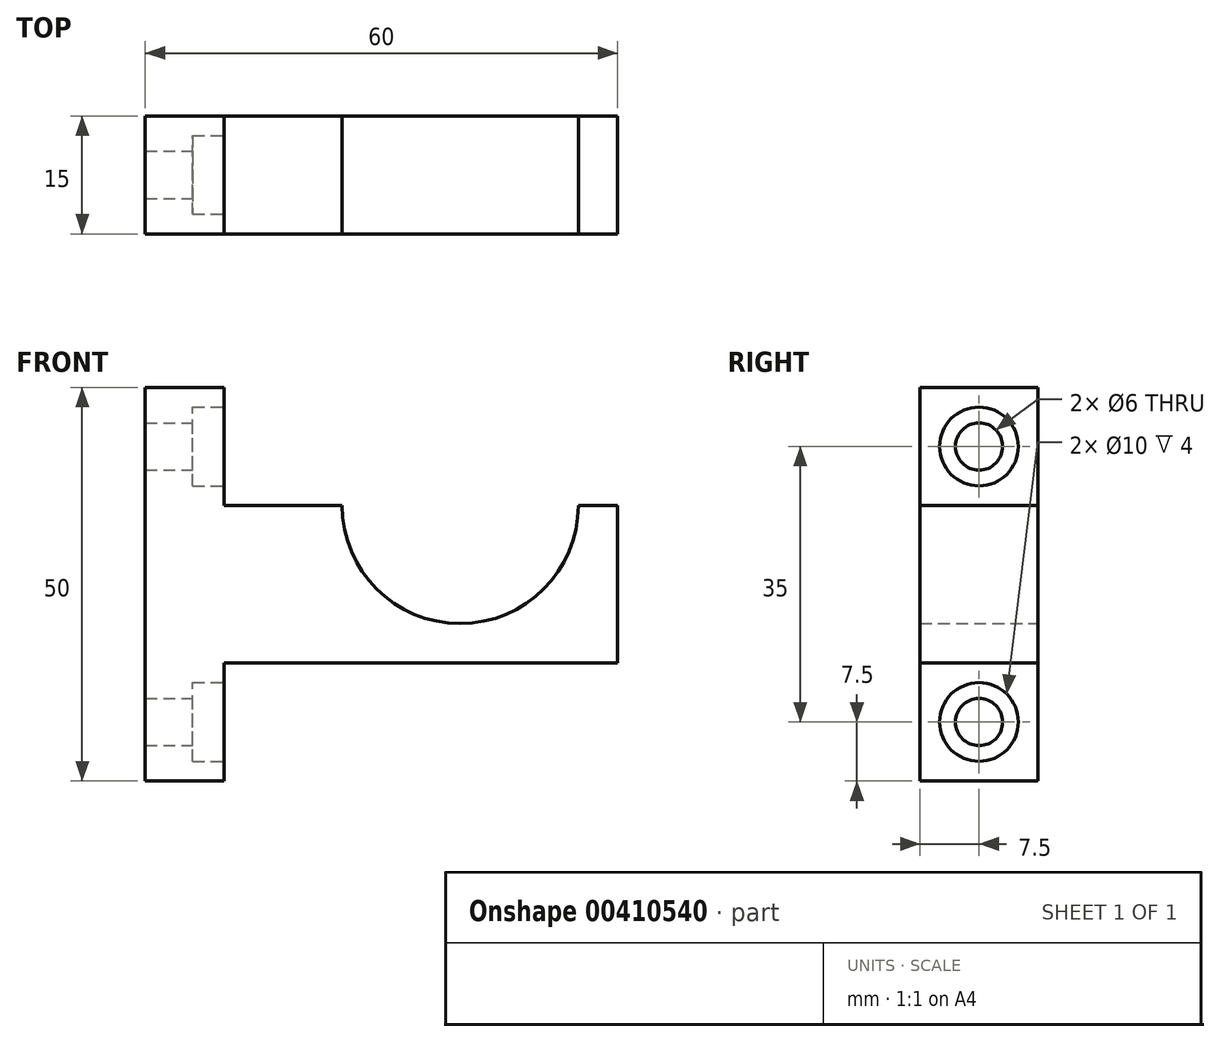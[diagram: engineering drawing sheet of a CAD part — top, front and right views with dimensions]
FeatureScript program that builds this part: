
annotation { "Feature Type Name" : "Feature", "Feature Type Description" : "" }
export const myFeature = defineFeature(function(context is Context, id is Id, definition is map)
    precondition{}
    {
        {
            var Q0;
            Q0=qCreatedBy(makeId("Front.planeOp"),FACE);
            var sketch = newSketch(context, id + "F0", { "sketchPlane" : qUnion([Q0])});
            skLineSegment(sketch, "E0.bottom", {"start": v(30, -25) * mm, "end": v(-30, -25) * mm});
            skLineSegment(sketch, "E0.top", {"start": v(30, 25) * mm, "end": v(-30, 25) * mm});
            skLineSegment(sketch, "E0.left", {"start": v(30, -25) * mm, "end": v(30, 25) * mm});
            skLineSegment(sketch, "E0.right", {"start": v(-30, -25) * mm, "end": v(-30, 25) * mm});
            skPoint(sketch, "E0.middle", {"position": v(0, 0) * mm});
            skPoint(sketch, "E1", {"position": v(10, 10) * mm});
            skCircle(sketch, "E2", {"center": v(10, 10) * mm, "radius": 15 * mm});
            skLineSegment(sketch, "E3", {"start": v(-30, 10) * mm, "end": v(30, 10) * mm});
            skLineSegment(sketch, "E4", {"start": v(-30, -10) * mm, "end": v(30, -10) * mm});
            skLineSegment(sketch, "E5", {"start": v(-20, 25) * mm, "end": v(-20, -25) * mm});
            skSolve(sketch);
        }
        {
            var Q0;
            {var subQ0=sQuery(id+"F0.wireOp",EDGE,"E0.right");var subQ1=sQuery(id+"F0.wireOp",EDGE,"E0.top");var subQ2=makeQuery(id+"F0.imprint","INTERSECT",VERTEX,{"derivedFrom":[subQ1,subQ0]});Q0=makeQuery(id+"F0.imprint","IMPRINT",FACE,{"disambiguationData":[TD([[makeQuery(id+"F0.imprint","IMPRINT",EDGE,{"disambiguationData":[TD([[subQ2,1.0]])],"derivedFrom":subQ1}),1.0]])]});}
            var Q1;
            {var subQ0=sQuery(id+"F0.wireOp",EDGE,"E3");var subQ1=sQuery(id+"F0.wireOp",EDGE,"E0.right");var subQ2=makeQuery(id+"F0.imprint","INTERSECT",VERTEX,{"derivedFrom":[subQ1,subQ0]});Q1=makeQuery(id+"F0.imprint","IMPRINT",FACE,{"disambiguationData":[TD([[makeQuery(id+"F0.imprint","IMPRINT",EDGE,{"disambiguationData":[TD([[subQ2,1.0]])],"derivedFrom":subQ1}),-1.0]])]});}
            var Q2;
            {var subQ0=sQuery(id+"F0.wireOp",EDGE,"E3");var subQ1=sQuery(id+"F0.wireOp",EDGE,"E0.left");var subQ2=makeQuery(id+"F0.imprint","INTERSECT",VERTEX,{"derivedFrom":[subQ1,subQ0]});Q2=makeQuery(id+"F0.imprint","IMPRINT",FACE,{"disambiguationData":[TD([[makeQuery(id+"F0.imprint","IMPRINT",EDGE,{"disambiguationData":[TD([[subQ2,1.0]])],"derivedFrom":subQ1}),1.0]])]});}
            var Q3;
            {var subQ0=sQuery(id+"F0.wireOp",EDGE,"E0.right");var subQ1=sQuery(id+"F0.wireOp",EDGE,"E0.bottom");var subQ2=makeQuery(id+"F0.imprint","INTERSECT",VERTEX,{"derivedFrom":[subQ1,subQ0]});Q3=makeQuery(id+"F0.imprint","IMPRINT",FACE,{"disambiguationData":[TD([[makeQuery(id+"F0.imprint","IMPRINT",EDGE,{"disambiguationData":[TD([[subQ2,1.0]])],"derivedFrom":subQ1}),-1.0]])]});}
            extrude(context, id + "F1", {"entities" : qUnion([Q0, Q1, Q2, Q3]), "depth" : 15 * mm});
        }
        {
            var Q0;
            {var subQ0=sQuery(id+"F0.wireOp",EDGE,"E5");Q0=makeQuery(id+"F1.opExtrude","SWEPT_FACE",FACE,{"disambiguationData":[OSD([subQ0]),TDD([makeQuery(id+"F0.imprint","IMPRINT",EDGE,{"disambiguationData":[TD([[makeQuery(id+"F0.imprint","INTERSECT",VERTEX,{"derivedFrom":[sQuery(id+"F0.wireOp",EDGE,"E0.top"),subQ0]}),-1.0]])],"derivedFrom":subQ0})])]});}
            var sketch = newSketch(context, id + "F2", { "sketchPlane" : qUnion([Q0])});
            skPoint(sketch, "E6", {"position": v(-7.5, 17.5) * mm});
            skPoint(sketch, "E6.positionSnap0", {"position": v(-7.5, 25) * mm});
            skCircle(sketch, "E7", {"center": v(-7.5, 17.5) * mm, "radius": 3 * mm});
            skSolve(sketch);
        }
        {
            var Q0;
            Q0=makeQuery(id+"F2.imprint","IMPRINT",FACE,{"disambiguationData":[TD([[makeQuery(id+"F2.imprint","IMPRINT",EDGE,{"derivedFrom":sQuery(id+"F2.wireOp",EDGE,"E7")}),1.0]])]});
            extrude(context, id + "F3", {"entities" : qUnion([Q0]), "operationType" : NewBodyOperationType.REMOVE, "endBound" : BoundingType.THROUGH_ALL, "oppositeDirection" : true, "depth" : 25 * mm});
        }
        {
            var Q0;
            {var subQ0=sQuery(id+"F0.wireOp",EDGE,"E5");Q0=makeQuery(id+"F1.opExtrude","SWEPT_FACE",FACE,{"disambiguationData":[OSD([subQ0]),TDD([makeQuery(id+"F0.imprint","IMPRINT",EDGE,{"disambiguationData":[TD([[makeQuery(id+"F0.imprint","INTERSECT",VERTEX,{"derivedFrom":[sQuery(id+"F0.wireOp",EDGE,"E0.top"),subQ0]}),-1.0]])],"derivedFrom":subQ0})])]});}
            var sketch = newSketch(context, id + "F4", { "sketchPlane" : qUnion([Q0])});
            skPoint(sketch, "E8", {"position": v(-7.5, 17.5) * mm});
            skCircle(sketch, "E9", {"center": v(-7.5, 17.5) * mm, "radius": 5 * mm});
            skSolve(sketch);
        }
        {
            var Q0;
            Q0=makeQuery(id+"F4.imprint","IMPRINT",FACE,{"disambiguationData":[TD([[makeQuery(id+"F4.imprint","IMPRINT",EDGE,{"derivedFrom":sQuery(id+"F4.wireOp",EDGE,"E9")}),1.0]])]});
            extrude(context, id + "F5", {"entities" : qUnion([Q0]), "operationType" : NewBodyOperationType.REMOVE, "oppositeDirection" : true, "depth" : 4 * mm});
        }
        {
            var Q0;
            {var subQ0=sQuery(id+"F0.wireOp",EDGE,"E5");Q0=makeQuery(id+"F1.opExtrude","SWEPT_FACE",FACE,{"disambiguationData":[OSD([subQ0]),TDD([makeQuery(id+"F0.imprint","IMPRINT",EDGE,{"disambiguationData":[TD([[makeQuery(id+"F0.imprint","INTERSECT",VERTEX,{"derivedFrom":[sQuery(id+"F0.wireOp",EDGE,"E0.bottom"),subQ0]}),1.0]])],"derivedFrom":subQ0})])]});}
            var sketch = newSketch(context, id + "F6", { "sketchPlane" : qUnion([Q0])});
            skPoint(sketch, "E10", {"position": v(-7.5, -17.5) * mm});
            skCircle(sketch, "E11", {"center": v(-7.5, -17.5) * mm, "radius": 3 * mm});
            skSolve(sketch);
        }
        {
            var Q0;
            Q0=makeQuery(id+"F6.imprint","IMPRINT",FACE,{"disambiguationData":[TD([[makeQuery(id+"F6.imprint","IMPRINT",EDGE,{"derivedFrom":sQuery(id+"F6.wireOp",EDGE,"E11")}),1.0]])]});
            extrude(context, id + "F7", {"entities" : qUnion([Q0]), "operationType" : NewBodyOperationType.REMOVE, "endBound" : BoundingType.THROUGH_ALL, "oppositeDirection" : true, "depth" : 25 * mm});
        }
        {
            var Q0;
            {var subQ0=sQuery(id+"F0.wireOp",EDGE,"E5");Q0=makeQuery(id+"F1.opExtrude","SWEPT_FACE",FACE,{"disambiguationData":[OSD([subQ0]),TDD([makeQuery(id+"F0.imprint","IMPRINT",EDGE,{"disambiguationData":[TD([[makeQuery(id+"F0.imprint","INTERSECT",VERTEX,{"derivedFrom":[sQuery(id+"F0.wireOp",EDGE,"E0.bottom"),subQ0]}),1.0]])],"derivedFrom":subQ0})])]});}
            var sketch = newSketch(context, id + "F8", { "sketchPlane" : qUnion([Q0])});
            skPoint(sketch, "E12", {"position": v(-7.5, -17.5) * mm});
            skCircle(sketch, "E13", {"center": v(-7.5, -17.5) * mm, "radius": 5 * mm});
            skSolve(sketch);
        }
        {
            var Q0;
            Q0=makeQuery(id+"F8.imprint","IMPRINT",FACE,{"disambiguationData":[TD([[makeQuery(id+"F8.imprint","IMPRINT",EDGE,{"derivedFrom":sQuery(id+"F8.wireOp",EDGE,"E13")}),1.0]])]});
            extrude(context, id + "F9", {"entities" : qUnion([Q0]), "operationType" : NewBodyOperationType.REMOVE, "oppositeDirection" : true, "depth" : 4 * mm});
        }
    });
